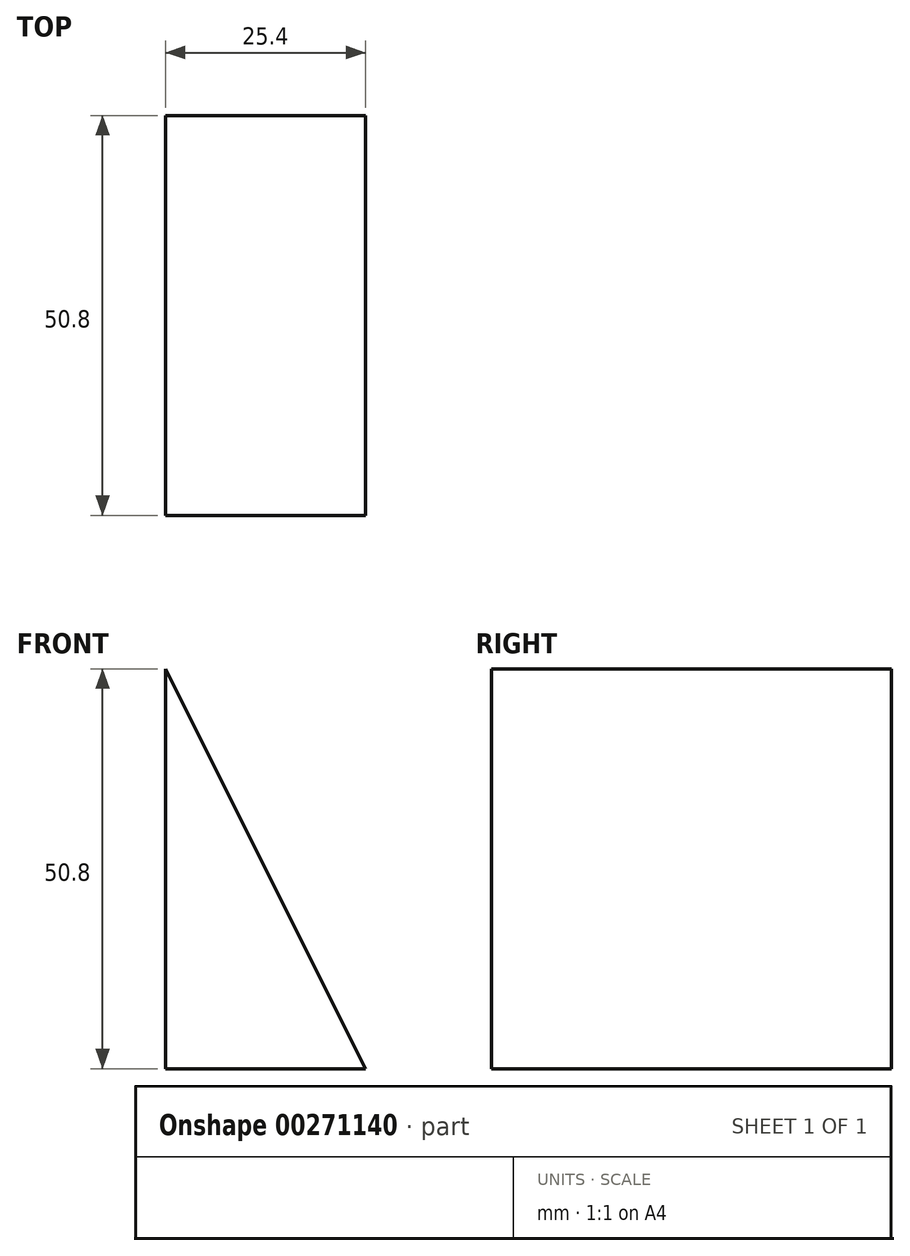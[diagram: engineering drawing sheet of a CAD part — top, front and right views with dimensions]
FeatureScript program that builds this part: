
annotation { "Feature Type Name" : "Feature", "Feature Type Description" : "" }
export const myFeature = defineFeature(function(context is Context, id is Id, definition is map)
    precondition{}
    {
        {
            var Q0;
            Q0=qCreatedBy(makeId("Front.planeOp"),FACE);
            var sketch = newSketch(context, id + "F0", { "sketchPlane" : qUnion([Q0])});
            skLineSegment(sketch, "E0", {"start": v(-29.03, 29.6) * mm, "end": v(-29.03, -21.2) * mm});
            skLineSegment(sketch, "E1", {"start": v(-29.03, -21.2) * mm, "end": v(-3.63, -21.2) * mm});
            skLineSegment(sketch, "E2", {"start": v(-3.63, -21.2) * mm, "end": v(-29.03, 29.6) * mm});
            skSolve(sketch);
        }
        {
            var Q0;
            Q0 = qSketchRegion(id + "F0", true);
            extrude(context, id + "F1", {"entities" : qUnion([Q0]), "depth" : 50.8 * mm});
        }
    });
